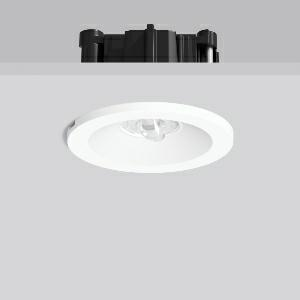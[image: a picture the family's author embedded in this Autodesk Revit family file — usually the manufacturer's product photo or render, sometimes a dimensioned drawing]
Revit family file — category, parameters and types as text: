
# Revit family: turia_l_672561_002_04_e1b3
name_source: partatom
category: Lighting Fixtures
units: mm (PartAtom-declared; Revit-internal decimal feet)

## family parameters
Cut with Voids When Loaded = No
Host = Face
Light Source = No
Part Type = Normal
Room Calculation Point = No
Round Connector Dimension = Use Diameter
Shared = No

## types (1)
- TURIA L (1 x LED Modul 765, 270 lm, 6500)
    Apparent Load = 5 VA
    CIE Flux Codes = 70 91 99 100 100
    Color Rendering = 70
    Color Temperature = 6500
    Default Elevation = 1800 mm
    Description = Series: TURIA L
Round emergency luminaire for escape route lighting. Housing: die-cast aluminium. Bezel ring: plastic. With asymmetrical beam plastic lenses for illuminating rescue facilities. Self-contained system with automatic self-test and feedback to the RZB monitoring system MULTIDIGIT. With enclosed separate ceiling mounting ring also suitable for ceiling cut-outs of Ø 68 mm. 
Colour: white
Diameter: 62 mm
Height: 3 mm
Cut-out diameter: 54-68 mm
Recess height: 76-162 mm
Luminaire: recess height: 42 mm
Weight: 430 g
Operating mode: non-maintained power mode
Duration time: 3 h
Lamp: LED
Socket: without socket
Colour temperature: 6500K
Colour rendering index (CRI): 70
System power: 5.2 W
Rated luminous flux: 270 lm
Luminous flux, emergency: 190 lm
System power, emergency: -
Control gear: Regulated power supply
Protection class: II
Type of protection: IP 20
    Height = 0 mm  [stored 0 ft]
    Lamp = 1 x LED Modul 765
    Lamp Light Flux = 270 lm
    Lamp count = 1
    Length = 62 mm  [stored 0.203412 ft]
    Lifetime = 50000 h
    Luminous efficacy = 52 lm/W
    Manufacturer = RZB
    ModVariant = No
    Model = 672561.002.04
    Mounting Place = Ceiling
    Mounting Type = Recessed
    Number of Poles = 1
    OnlyDefault = Yes
    Power Factor = 1
    Product Name = TURIA L
    Product group = Recessed ceiling luminaires
    ProductGroupID = 405
    Protection Class = Protection class II
    Protection Degree = IP 20
    RLX_Detail_Level = 1
    RLX_Emergency_Light_Flux = 190 lm
    RLX_Emergency_Type = 3
    RLX_Emergency_Type_DB = Yes
    RlxData = <blob elided: 55441 chars, md5=23765d8d>
    Socket = socket
    Standby Power = 0 W
    System Light Flux = 270 lm
    System Power = 5 W
    Type Comments = Product without accessories
    Type Image = 672561.002.jpg
    URL = http://relux.com
    VarID = ---
    Voltage = 230 V
    Voltage Range = 220-240 V
    Weight = 0.00 kg
    Width = 0 mm  [stored 0 ft]

note: [stored X ft] marks values corroborated as IEEE doubles in the binary element streams (Revit-internal decimal feet)

## geometry (parser evidence)
native form markers: Blend x4, Sweep x10
no freeform markers — native parametric forms only
